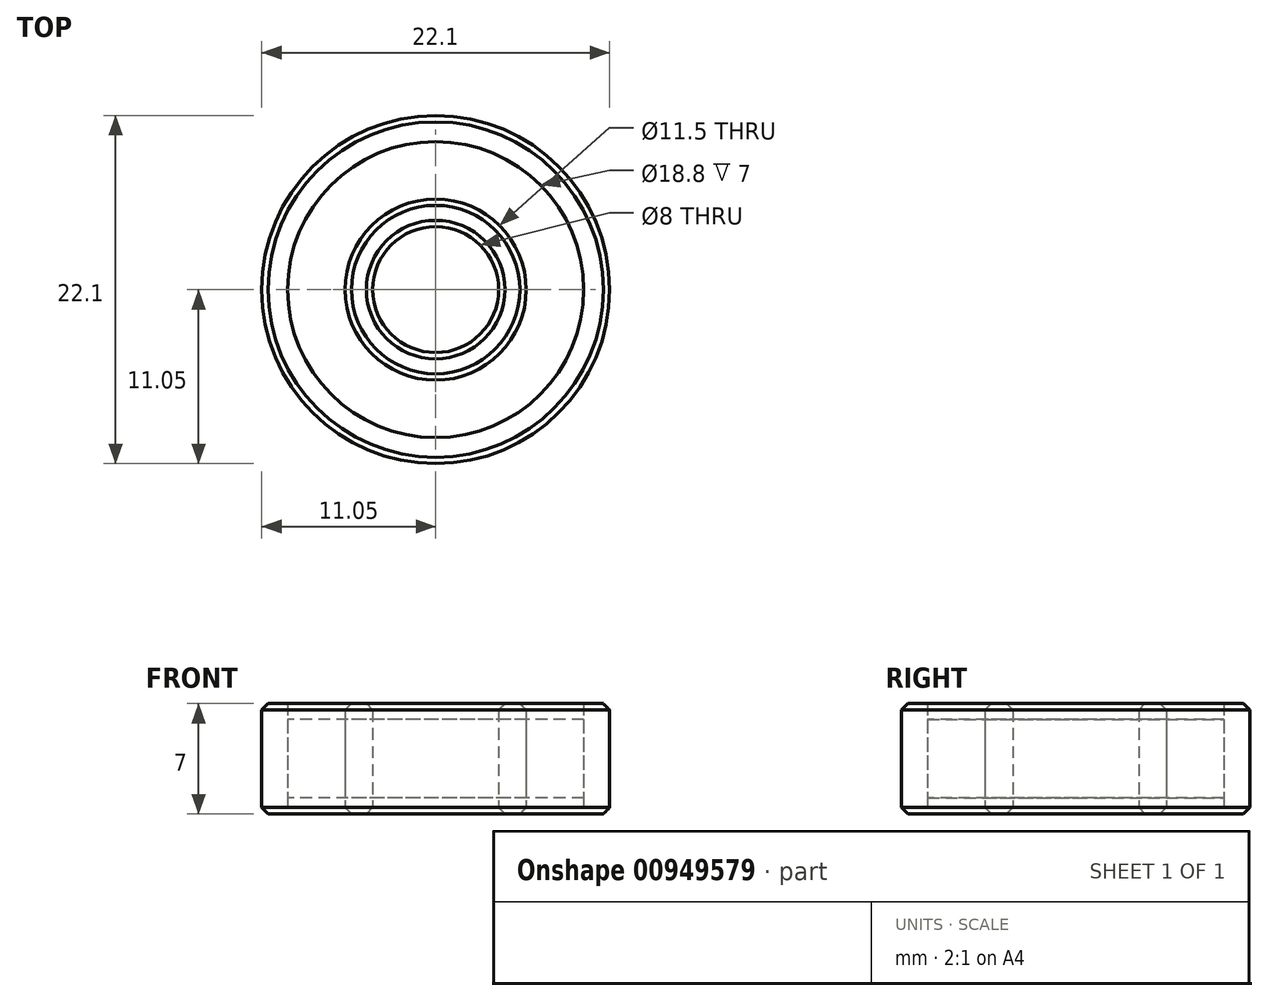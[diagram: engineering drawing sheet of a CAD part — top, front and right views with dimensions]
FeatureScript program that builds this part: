
annotation { "Feature Type Name" : "Feature", "Feature Type Description" : "" }
export const myFeature = defineFeature(function(context is Context, id is Id, definition is map)
    precondition{}
    {
        {
            var Q0;
            Q0=qCreatedBy(makeId("Top.planeOp"),FACE);
            var sketch = newSketch(context, id + "F0", { "sketchPlane" : qUnion([Q0])});
            skCircle(sketch, "E0", {"center": v(0, 0) * mm, "radius": 11.05 * mm});
            skCircle(sketch, "E1", {"center": v(0, 0) * mm, "radius": 4 * mm});
            skCircle(sketch, "E2", {"center": v(0, 0) * mm, "radius": 5.75 * mm});
            skCircle(sketch, "E3", {"center": v(0, 0) * mm, "radius": 9.4 * mm});
            skSolve(sketch);
        }
        {
            var Q0;
            Q0=makeQuery(id+"F0.imprint","IMPRINT",FACE,{"disambiguationData":[TD([[makeQuery(id+"F0.imprint","IMPRINT",EDGE,{"derivedFrom":sQuery(id+"F0.wireOp",EDGE,"E0")}),1.0]])]});
            var Q1;
            Q1=makeQuery(id+"F0.imprint","IMPRINT",FACE,{"disambiguationData":[TD([[makeQuery(id+"F0.imprint","IMPRINT",EDGE,{"derivedFrom":sQuery(id+"F0.wireOp",EDGE,"E1")}),-1.0]])]});
            extrude(context, id + "F1", {"entities" : qUnion([Q0, Q1]), "endBound" : BoundingType.SYMMETRIC, "depth" : 7 * mm, "offsetDistance" : 25 * mm});
        }
        {
            var Q0;
            Q0=makeQuery(id+"F0.imprint","IMPRINT",FACE,{"disambiguationData":[TD([[makeQuery(id+"F0.imprint","IMPRINT",EDGE,{"derivedFrom":sQuery(id+"F0.wireOp",EDGE,"E2")}),-1.0]])]});
            extrude(context, id + "F2", {"entities" : qUnion([Q0]), "endBound" : BoundingType.SYMMETRIC, "depth" : 5 * mm, "offsetDistance" : 25 * mm});
        }
        {
            var Q0;
            Q0=makeQuery(id+"F1.opExtrude","CAP_EDGE",EDGE,{"disambiguationData":[OSD([sQuery(id+"F0.wireOp",EDGE,"E0")])],"isStart":false});
            var Q1;
            Q1=makeQuery(id+"F1.opExtrude","CAP_EDGE",EDGE,{"disambiguationData":[OSD([sQuery(id+"F0.wireOp",EDGE,"E0")])],"isStart":true});
            var Q2;
            Q2=makeQuery(id+"F1.opExtrude","CAP_EDGE",EDGE,{"disambiguationData":[OSD([sQuery(id+"F0.wireOp",EDGE,"E1")])],"isStart":false});
            var Q3;
            Q3=makeQuery(id+"F1.opExtrude","CAP_EDGE",EDGE,{"disambiguationData":[OSD([sQuery(id+"F0.wireOp",EDGE,"E2")])],"isStart":false});
            var Q4;
            Q4=makeQuery(id+"F1.opExtrude","CAP_FACE",FACE,{"disambiguationData":[OSD([sQuery(id+"F0.wireOp",EDGE,"E1"),sQuery(id+"F0.wireOp",EDGE,"E2")])],"isStart":true});
            chamfer(context, id + "F3", {"entities" : qUnion([Q0, Q1, Q2, Q3, Q4]), "width" : .4 * mm, "tangentPropagation" : true});
        }
    });
